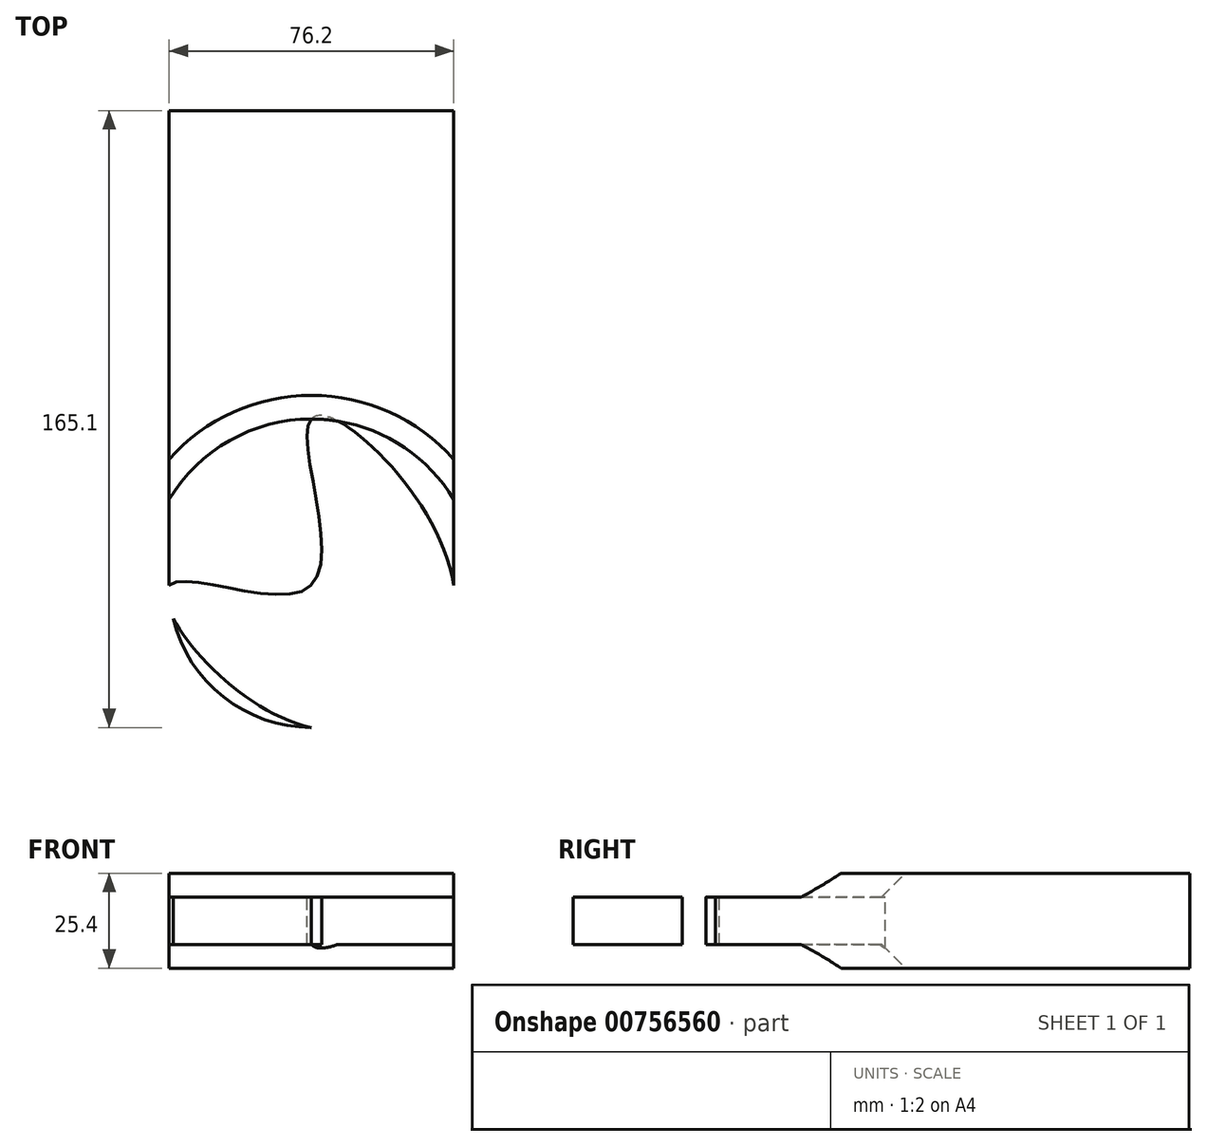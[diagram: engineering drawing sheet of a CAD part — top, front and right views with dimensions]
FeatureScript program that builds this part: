
annotation { "Feature Type Name" : "Feature", "Feature Type Description" : "" }
export const myFeature = defineFeature(function(context is Context, id is Id, definition is map)
    precondition{}
    {
        {
            var Q0;
            Q0=qCreatedBy(makeId("Top.planeOp"),FACE);
            var sketch = newSketch(context, id + "F0", { "sketchPlane" : qUnion([Q0])});
            skLineSegment(sketch, "E0.bottom", {"start": v(-38.1, 0) * mm, "end": v(38.1, 0) * mm});
            skLineSegment(sketch, "E0.top", {"start": v(-38.1, 127) * mm, "end": v(38.1, 127) * mm});
            skLineSegment(sketch, "E0.left", {"start": v(-38.1, 0) * mm, "end": v(-38.1, 127) * mm});
            skLineSegment(sketch, "E0.right", {"start": v(38.1, 0) * mm, "end": v(38.1, 127) * mm});
            skCircle(sketch, "E1", {"center": v(0, 0) * mm, "radius": 38.1 * mm});
            skSolve(sketch);
        }
        {
            var Q0;
            Q0=makeQuery(id+"F0.imprint","IMPRINT",FACE,{"disambiguationData":[TD([[makeQuery(id+"F0.imprint","IMPRINT",EDGE,{"derivedFrom":sQuery(id+"F0.wireOp",EDGE,"E0.top")}),-1.0]])]});
            extrude(context, id + "F1", {"entities" : qUnion([Q0]), "endBound" : BoundingType.SYMMETRIC, "depth" : 25.4 * mm, "offsetDistance" : 25.4 * mm});
        }
        {
            var Q0;
            Q0 = qSketchRegion(id + "F0", true);
            extrude(context, id + "F2", {"entities" : qUnion([Q0]), "operationType" : NewBodyOperationType.ADD, "endBound" : BoundingType.SYMMETRIC, "depth" : 12.7 * mm, "offsetDistance" : 25.4 * mm});
        }
        {
            var Q0;
            Q0=makeQuery(id+"F1.opExtrude","CAP_EDGE",EDGE,{"disambiguationData":[OSD([sQuery(id+"F0.wireOp",EDGE,"E1")])],"isStart":true});
            chamfer(context, id + "F3", {"entities" : qUnion([Q0]), "width" : 12.7 * mm, "tangentPropagation" : true});
        }
        {
            var Q0;
            Q0=makeQuery(id+"F1.opExtrude","CAP_EDGE",EDGE,{"disambiguationData":[OSD([sQuery(id+"F0.wireOp",EDGE,"E1")])],"isStart":false});
            chamfer(context, id + "F4", {"entities" : qUnion([Q0]), "width" : 12.7 * mm, "tangentPropagation" : true});
        }
        {
            var Q0;
            Q0=makeQuery(id+"F2.opExtrude","CAP_FACE",FACE,{"disambiguationData":[OSD([sQuery(id+"F0.wireOp",EDGE,"E0.top"),sQuery(id+"F0.wireOp",EDGE,"E0.left"),sQuery(id+"F0.wireOp",EDGE,"E0.right"),sQuery(id+"F0.wireOp",EDGE,"E1")])],"isStart":false});
            var sketch = newSketch(context, id + "F5", { "sketchPlane" : qUnion([Q0])});
            skFitSpline(sketch, "E2", {"points": [v(0, 0) * mm, v(0, 44.45) * mm, v(38.1, 0) * mm, v(0, -38.1) * mm, v(-38.1, 0) * mm, v(0, 0) * mm]});
            skSolve(sketch);
        }
        {
            var Q0;
            Q0 = qSketchRegion(id + "F5", true);
            extrude(context, id + "F6", {"entities" : qUnion([Q0]), "operationType" : NewBodyOperationType.REMOVE, "endBound" : BoundingType.THROUGH_ALL, "oppositeDirection" : true, "depth" : 25.4 * mm, "offsetDistance" : 25.4 * mm});
        }
    });
